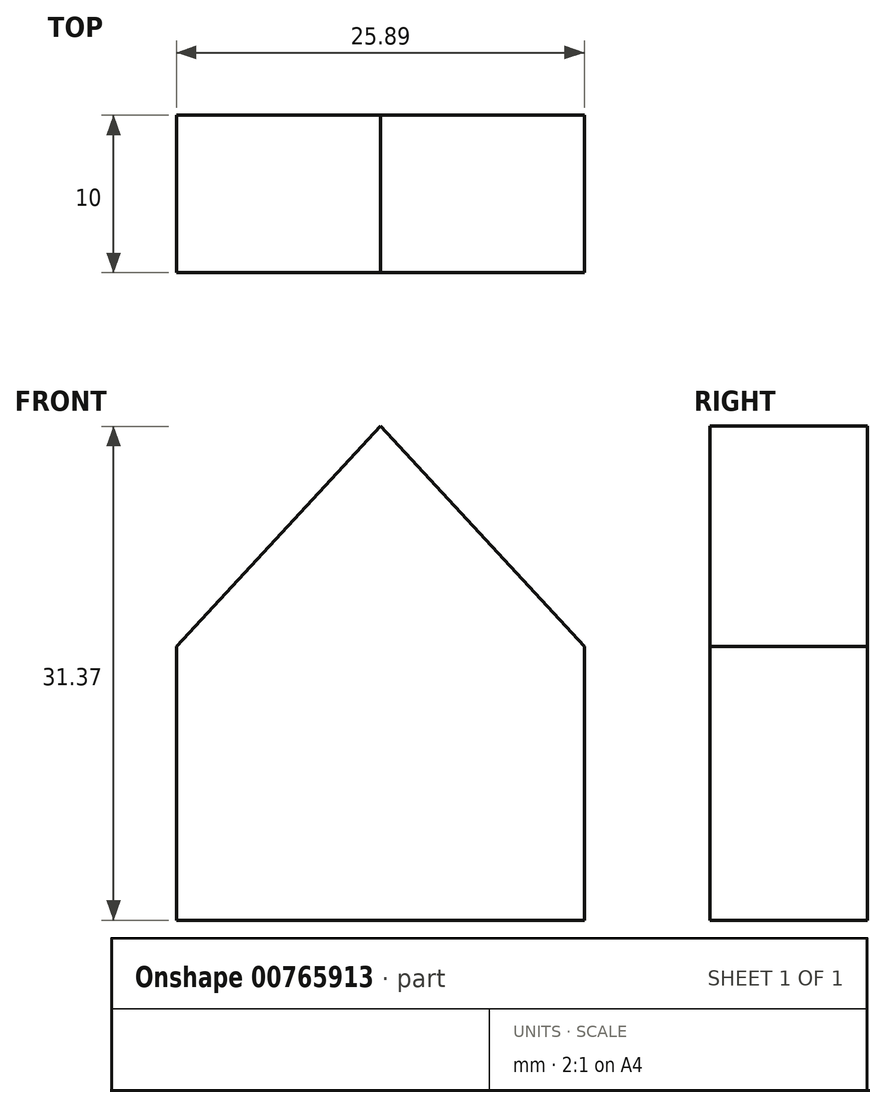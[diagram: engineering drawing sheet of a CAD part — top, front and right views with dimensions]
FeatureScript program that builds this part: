
annotation { "Feature Type Name" : "Feature", "Feature Type Description" : "" }
export const myFeature = defineFeature(function(context is Context, id is Id, definition is map)
    precondition{}
    {
        {
            var Q0;
            Q0=qCreatedBy(makeId("Front.planeOp"),FACE);
            var sketch = newSketch(context, id + "F0", { "sketchPlane" : qUnion([Q0])});
            skLineSegment(sketch, "E0.bottom", {"start": v(0, 0) * mm, "end": v(-25.89, 0) * mm});
            skLineSegment(sketch, "E0.top", {"start": v(0, 17.39) * mm, "end": v(-25.89, 17.39) * mm});
            skLineSegment(sketch, "E0.left", {"start": v(0, 0) * mm, "end": v(0, 17.39) * mm});
            skLineSegment(sketch, "E0.right", {"start": v(-25.89, 0) * mm, "end": v(-25.89, 17.39) * mm});
            skLineSegment(sketch, "E1", {"start": v(-25.89, 17.39) * mm, "end": v(-12.94, 31.37) * mm});
            skLineSegment(sketch, "E2", {"start": v(-12.94, 31.37) * mm, "end": v(-12.94, 31.37) * mm});
            skLineSegment(sketch, "E3", {"start": v(-12.94, 31.37) * mm, "end": v(0, 17.39) * mm});
            skLineSegment(sketch, "E4", {"start": v(-12.94, 31.37) * mm, "end": v(-12.94, 17.39) * mm});
            skPoint(sketch, "E4.endSnap0", {"position": v(-12.94, 17.39) * mm});
            skSolve(sketch);
        }
        {
            var Q0;
            Q0 = qSketchRegion(id + "F0", true);
            extrude(context, id + "F1", {"entities" : qUnion([Q0]), "depth" : 10 * mm, "offsetDistance" : 25.4 * mm});
        }
    });
